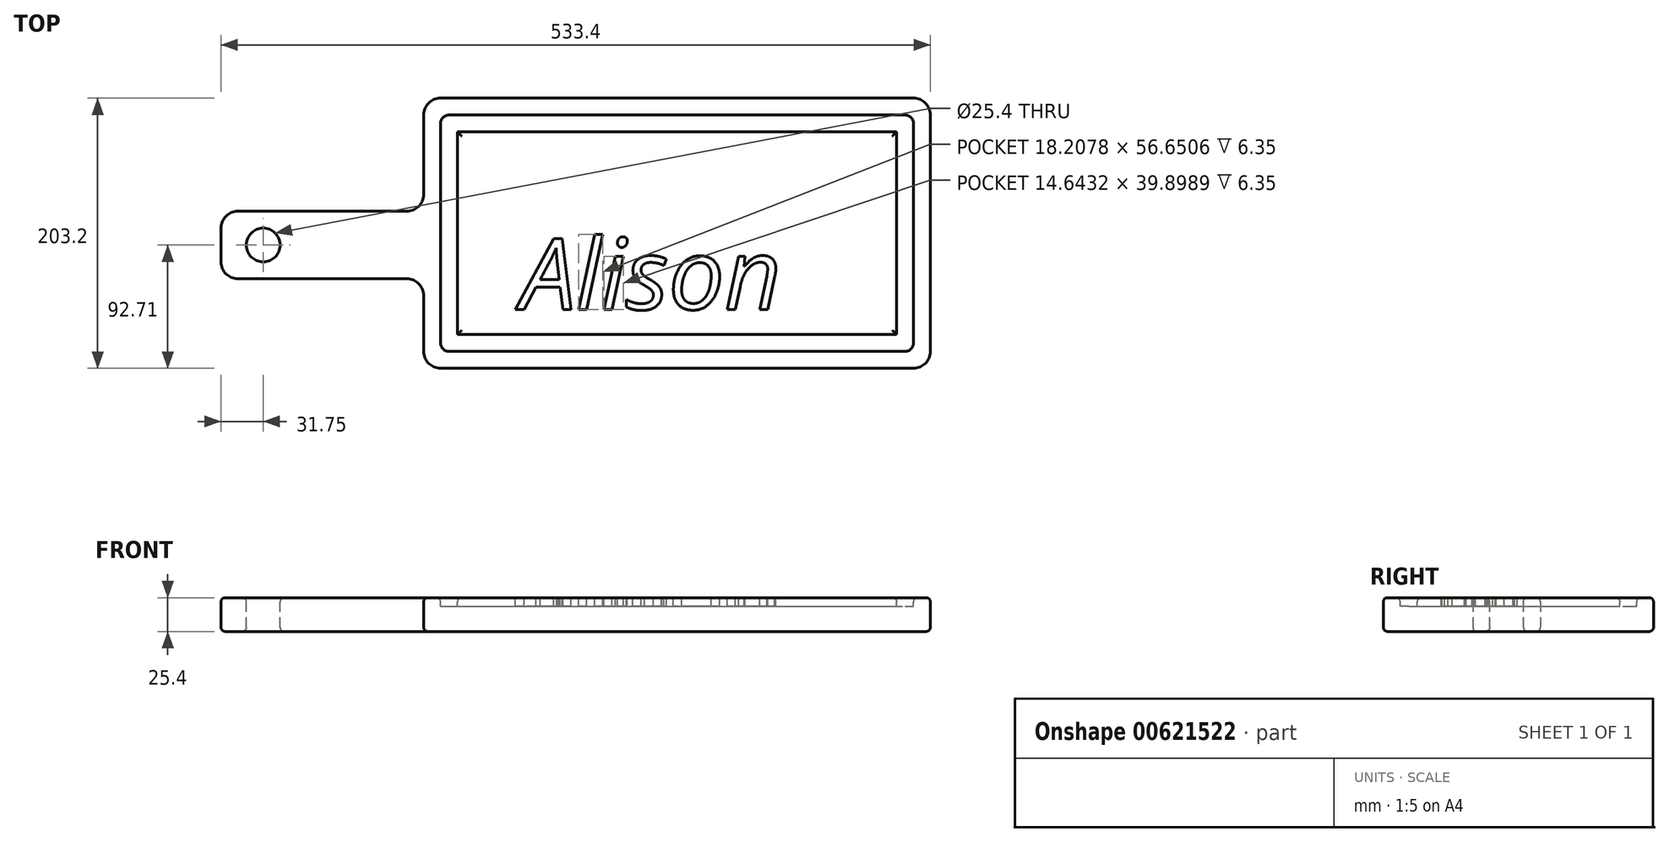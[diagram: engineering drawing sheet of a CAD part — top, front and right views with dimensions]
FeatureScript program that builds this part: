
annotation { "Feature Type Name" : "Feature", "Feature Type Description" : "" }
export const myFeature = defineFeature(function(context is Context, id is Id, definition is map)
    precondition{}
    {
        {
            var Q0;
            Q0=qCreatedBy(makeId("Top.planeOp"),FACE);
            var sketch = newSketch(context, id + "F0", { "sketchPlane" : qUnion([Q0])});
            skLineSegment(sketch, "E0.bottom", {"start": v(0, 0) * mm, "end": v(381, 0) * mm});
            skLineSegment(sketch, "E0.top", {"start": v(0, 203.2) * mm, "end": v(381, 203.2) * mm});
            skLineSegment(sketch, "E0.left", {"start": v(0, 0) * mm, "end": v(0, 203.2) * mm});
            skLineSegment(sketch, "E0.right", {"start": v(381, 0) * mm, "end": v(381, 203.2) * mm});
            skLineSegment(sketch, "E1.bottom", {"start": v(0, 118.11) * mm, "end": v(-152.4, 118.1) * mm});
            skLineSegment(sketch, "E1.top", {"start": v(0, 67.3) * mm, "end": v(-152.4, 67.3) * mm});
            skLineSegment(sketch, "E1.left", {"start": v(0, 118.11) * mm, "end": v(0, 67.3) * mm});
            skLineSegment(sketch, "E1.right", {"start": v(-152.4, 118.1) * mm, "end": v(-152.4, 67.3) * mm});
            skSolve(sketch);
        }
        {
            var Q0;
            {var subQ3=sQuery(id+"F0.wireOp",EDGE,"E0.bottom");Q0=makeQuery(id+"F0.imprint","IMPRINT",FACE,{"disambiguationData":[TD([[makeQuery(id+"F0.imprint","IMPRINT",EDGE,{"derivedFrom":subQ3}),1.0]])]});}
            var Q1;
            Q1=makeQuery(id+"F0.imprint","IMPRINT",FACE,{"disambiguationData":[TD([[makeQuery(id+"F0.imprint","IMPRINT",EDGE,{"derivedFrom":sQuery(id+"F0.wireOp",EDGE,"E1.bottom")}),1.0]])]});
            extrude(context, id + "F1", {"entities" : qUnion([Q0, Q1]), "depth" : 25.4 * mm, "offsetDistance" : 25.4 * mm});
        }
        {
            var Q0;
            Q0=makeQuery(id+"F1.opExtrude","CAP_FACE",FACE,{"disambiguationData":[OSD([sQuery(id+"F0.wireOp",EDGE,"E0.bottom"),sQuery(id+"F0.wireOp",EDGE,"E0.top"),sQuery(id+"F0.wireOp",EDGE,"E0.left"),sQuery(id+"F0.wireOp",EDGE,"E0.right"),sQuery(id+"F0.wireOp",EDGE,"E1.bottom"),sQuery(id+"F0.wireOp",EDGE,"E1.top"),sQuery(id+"F0.wireOp",EDGE,"E1.right")])],"isStart":false});
            var sketch = newSketch(context, id + "F2", { "sketchPlane" : qUnion([Q0])});
            skCircle(sketch, "E2", {"center": v(-120.65, 92.7) * mm, "radius": 12.7 * mm});
            skSolve(sketch);
        }
        {
            var Q0;
            Q0 = qSketchRegion(id + "F2", true);
            extrude(context, id + "F3", {"entities" : qUnion([Q0]), "operationType" : NewBodyOperationType.REMOVE, "oppositeDirection" : true, "depth" : 25.4 * mm, "offsetDistance" : 25.4 * mm});
        }
        {
            var Q0;
            Q0=makeQuery(id+"F1.opExtrude","CAP_FACE",FACE,{"disambiguationData":[OSD([sQuery(id+"F0.wireOp",EDGE,"E0.bottom"),sQuery(id+"F0.wireOp",EDGE,"E0.top"),sQuery(id+"F0.wireOp",EDGE,"E0.left"),sQuery(id+"F0.wireOp",EDGE,"E0.right"),sQuery(id+"F0.wireOp",EDGE,"E1.bottom"),sQuery(id+"F0.wireOp",EDGE,"E1.top"),sQuery(id+"F0.wireOp",EDGE,"E1.right")])],"isStart":false});
            var sketch = newSketch(context, id + "F4", { "sketchPlane" : qUnion([Q0])});
            skLineSegment(sketch, "E3.0", {"start": v(12.7, 12.7) * mm, "end": v(12.7, 67.3) * mm});
            skLineSegment(sketch, "E3.1", {"start": v(12.7, 118.11) * mm, "end": v(12.7, 190.5) * mm});
            skLineSegment(sketch, "E3.2", {"start": v(12.7, 190.5) * mm, "end": v(368.3, 190.5) * mm});
            skLineSegment(sketch, "E3.3", {"start": v(368.3, 12.7) * mm, "end": v(368.3, 190.5) * mm});
            skLineSegment(sketch, "E3.4", {"start": v(12.7, 12.7) * mm, "end": v(368.3, 12.7) * mm});
            skLineSegment(sketch, "E4", {"start": v(12.7, 118.11) * mm, "end": v(12.7, 67.3) * mm});
            skLineSegment(sketch, "E5.0", {"start": v(25.4, 118.11) * mm, "end": v(25.4, 177.8) * mm});
            skLineSegment(sketch, "E5.1", {"start": v(355.6, 25.4) * mm, "end": v(355.6, 177.8) * mm});
            skLineSegment(sketch, "E5.2", {"start": v(25.4, 25.4) * mm, "end": v(355.6, 25.4) * mm});
            skLineSegment(sketch, "E5.3", {"start": v(25.4, 177.8) * mm, "end": v(355.6, 177.8) * mm});
            skLineSegment(sketch, "E5.4", {"start": v(25.4, 25.4) * mm, "end": v(25.4, 67.3) * mm});
            skLineSegment(sketch, "E5.5", {"start": v(25.4, 118.11) * mm, "end": v(25.4, 67.3) * mm});
            skSolve(sketch);
        }
        {
            var Q0;
            Q0=makeQuery(id+"F4.imprint","IMPRINT",FACE,{"disambiguationData":[TD([[makeQuery(id+"F4.imprint","IMPRINT",EDGE,{"derivedFrom":sQuery(id+"F4.wireOp",EDGE,"E3.0")}),-1.0]])]});
            extrude(context, id + "F5", {"entities" : qUnion([Q0]), "operationType" : NewBodyOperationType.REMOVE, "oppositeDirection" : true, "depth" : 6.35 * mm, "offsetDistance" : 25.4 * mm});
        }
        {
            var Q0;
            Q0=makeQuery(id+"F5.boolean.opBoolean","COPY",EDGE,{"derivedFrom":makeQuery(id+"F5.opExtrude","SWEPT_EDGE",EDGE,{"disambiguationData":[OSD([sQuery(id+"F4.wireOp",EDGE,"E3.1"),sQuery(id+"F4.wireOp",EDGE,"E3.2")])]})});
            var Q1;
            Q1=makeQuery(id+"F5.boolean.opBoolean","COPY",EDGE,{"derivedFrom":makeQuery(id+"F5.opExtrude","SWEPT_EDGE",EDGE,{"disambiguationData":[OSD([sQuery(id+"F4.wireOp",EDGE,"E3.2"),sQuery(id+"F4.wireOp",EDGE,"E3.3")])]})});
            var Q2;
            Q2=makeQuery(id+"F5.boolean.opBoolean","COPY",EDGE,{"derivedFrom":makeQuery(id+"F5.opExtrude","SWEPT_EDGE",EDGE,{"disambiguationData":[OSD([sQuery(id+"F4.wireOp",EDGE,"E3.3"),sQuery(id+"F4.wireOp",EDGE,"E3.4")])]})});
            var Q3;
            Q3=makeQuery(id+"F5.boolean.opBoolean","COPY",EDGE,{"derivedFrom":makeQuery(id+"F5.opExtrude","SWEPT_EDGE",EDGE,{"disambiguationData":[OSD([sQuery(id+"F4.wireOp",EDGE,"E3.0"),sQuery(id+"F4.wireOp",EDGE,"E3.4")])]})});
            fillet(context, id + "F6", {"entities" : qUnion([Q0, Q1, Q2, Q3]), "radius" : 6.35 * mm, "tangentPropagation" : true, "allowEdgeOverflow" : false});
        }
        {
            var Q0;
            Q0=makeQuery(id+"F1.opExtrude","SWEPT_EDGE",EDGE,{"disambiguationData":[OSD([sQuery(id+"F0.wireOp",EDGE,"E0.top"),sQuery(id+"F0.wireOp",EDGE,"E0.right")])]});
            var Q1;
            Q1=makeQuery(id+"F1.opExtrude","SWEPT_EDGE",EDGE,{"disambiguationData":[OSD([sQuery(id+"F0.wireOp",EDGE,"E0.top"),sQuery(id+"F0.wireOp",EDGE,"E0.left")])]});
            var Q2;
            Q2=makeQuery(id+"F1.opExtrude","SWEPT_EDGE",EDGE,{"disambiguationData":[OSD([sQuery(id+"F0.wireOp",EDGE,"E0.bottom"),sQuery(id+"F0.wireOp",EDGE,"E0.right")])]});
            var Q3;
            Q3=makeQuery(id+"F1.opExtrude","SWEPT_EDGE",EDGE,{"disambiguationData":[OSD([sQuery(id+"F0.wireOp",EDGE,"E0.bottom"),sQuery(id+"F0.wireOp",EDGE,"E0.left")])]});
            var Q4;
            Q4=makeQuery(id+"F1.opExtrude","SWEPT_EDGE",EDGE,{"disambiguationData":[OSD([sQuery(id+"F0.wireOp",EDGE,"E1.top"),sQuery(id+"F0.wireOp",EDGE,"E1.right")])]});
            var Q5;
            Q5=makeQuery(id+"F1.opExtrude","SWEPT_EDGE",EDGE,{"disambiguationData":[OSD([sQuery(id+"F0.wireOp",EDGE,"E1.bottom"),sQuery(id+"F0.wireOp",EDGE,"E1.right")])]});
            var Q6;
            Q6=makeQuery(id+"F1.opExtrude","SWEPT_EDGE",EDGE,{"disambiguationData":[OSD([sQuery(id+"F0.wireOp",EDGE,"E0.left"),sQuery(id+"F0.wireOp",EDGE,"E1.bottom"),sQuery(id+"F0.wireOp",EDGE,"E1.left")])]});
            var Q7;
            Q7=makeQuery(id+"F1.opExtrude","SWEPT_EDGE",EDGE,{"disambiguationData":[OSD([sQuery(id+"F0.wireOp",EDGE,"E0.left"),sQuery(id+"F0.wireOp",EDGE,"E1.top"),sQuery(id+"F0.wireOp",EDGE,"E1.left")])]});
            fillet(context, id + "F7", {"entities" : qUnion([Q0, Q1, Q2, Q3, Q4, Q5, Q6, Q7]), "radius" : 12.7 * mm, "tangentPropagation" : true, "allowEdgeOverflow" : false});
        }
        {
            var Q0;
            Q0=makeQuery(id+"F5.boolean.opBoolean","SPLIT",FACE,{"disambiguationData":[TD([makeQuery(id+"F5.opExtrude","SWEPT_FACE",FACE,{"disambiguationData":[OSD([sQuery(id+"F4.wireOp",EDGE,"E5.1")])]})])],"derivedFrom":makeQuery(id+"F1.opExtrude","CAP_FACE",FACE,{"disambiguationData":[OSD([sQuery(id+"F0.wireOp",EDGE,"E0.bottom"),sQuery(id+"F0.wireOp",EDGE,"E0.top"),sQuery(id+"F0.wireOp",EDGE,"E0.left"),sQuery(id+"F0.wireOp",EDGE,"E0.right"),sQuery(id+"F0.wireOp",EDGE,"E1.bottom"),sQuery(id+"F0.wireOp",EDGE,"E1.top"),sQuery(id+"F0.wireOp",EDGE,"E1.right")])],"isStart":false})});
            var Q1;
            {var subQ0=sQuery(id+"F0.wireOp",EDGE,"E1.right");var subQ1=sQuery(id+"F0.wireOp",EDGE,"E1.top");var subQ2=sQuery(id+"F0.wireOp",EDGE,"E1.bottom");var subQ3=sQuery(id+"F0.wireOp",EDGE,"E0.right");var subQ4=sQuery(id+"F0.wireOp",EDGE,"E0.bottom");var subQ5=sQuery(id+"F0.wireOp",EDGE,"E0.left");var subQ6=sQuery(id+"F0.wireOp",EDGE,"E0.top");Q1=makeQuery(id+"F5.boolean.opBoolean","SPLIT",FACE,{"disambiguationData":[TD([makeQuery(id+"F1.opExtrude","SWEPT_FACE",FACE,{"disambiguationData":[OSD([subQ4])]})])],"derivedFrom":makeQuery(id+"F1.opExtrude","CAP_FACE",FACE,{"disambiguationData":[OSD([subQ4,subQ6,subQ5,subQ3,subQ2,subQ1,subQ0])],"isStart":false})});}
            var Q2;
            Q2=makeQuery(id+"F1.opExtrude","CAP_FACE",FACE,{"disambiguationData":[OSD([sQuery(id+"F0.wireOp",EDGE,"E0.bottom"),sQuery(id+"F0.wireOp",EDGE,"E0.top"),sQuery(id+"F0.wireOp",EDGE,"E0.left"),sQuery(id+"F0.wireOp",EDGE,"E0.right"),sQuery(id+"F0.wireOp",EDGE,"E1.bottom"),sQuery(id+"F0.wireOp",EDGE,"E1.top"),sQuery(id+"F0.wireOp",EDGE,"E1.right")])],"isStart":true});
            fillet(context, id + "F8", {"entities" : qUnion([Q0, Q1, Q2]), "radius" : 3.17 * mm, "tangentPropagation" : true, "allowEdgeOverflow" : false});
        }
        {
            var Q0;
            Q0=makeQuery(id+"F5.boolean.opBoolean","SPLIT",FACE,{"disambiguationData":[TD([makeQuery(id+"F5.opExtrude","SWEPT_FACE",FACE,{"disambiguationData":[OSD([sQuery(id+"F4.wireOp",EDGE,"E5.1")])]})])],"derivedFrom":makeQuery(id+"F1.opExtrude","CAP_FACE",FACE,{"disambiguationData":[OSD([sQuery(id+"F0.wireOp",EDGE,"E0.bottom"),sQuery(id+"F0.wireOp",EDGE,"E0.top"),sQuery(id+"F0.wireOp",EDGE,"E0.left"),sQuery(id+"F0.wireOp",EDGE,"E0.right"),sQuery(id+"F0.wireOp",EDGE,"E1.bottom"),sQuery(id+"F0.wireOp",EDGE,"E1.top"),sQuery(id+"F0.wireOp",EDGE,"E1.right")])],"isStart":false})});
            var sketch = newSketch(context, id + "F9", { "sketchPlane" : qUnion([Q0])});
            skText(sketch, "E6", { "text": "Alison", "fontName": "OpenSans-Italic.ttf"});
            const initialGuessF9  = {"E6": [0.07302, 0.04423, 1, 0, 0.05368]};
            skSetInitialGuess(sketch, initialGuessF9);
            skSolve(sketch);
        }
        {
            var Q0;
            Q0 = qSketchRegion(id + "F9", true);
            extrude(context, id + "F10", {"entities" : qUnion([Q0]), "operationType" : NewBodyOperationType.REMOVE, "oppositeDirection" : true, "depth" : 6.35 * mm, "offsetDistance" : 25.4 * mm});
        }
    });
